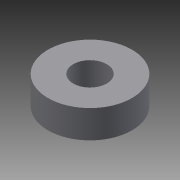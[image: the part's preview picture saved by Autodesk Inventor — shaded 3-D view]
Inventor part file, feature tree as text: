
AUTODESK INVENTOR PART (.ipt)
format: ipt  version: 2013 SP2 (Build 170200200, 200)  size: 74,240 bytes
history: native  units: mm
features: extrude x1, sketch x1
ambient origin geometry x8: Origin, YZ Plane, XZ Plane, XY Plane, X Axis, Y Axis, Z Axis, Center Point
bodies: Solid1 (feature_tree)
feature tree (2):
  extrude  "Extrusion1"  Depth=6.0mm
  sketch  "Sketch1"  dims[d0=15.0mm d2=6.0mm d3=5.0mm d4=0.0mm]
